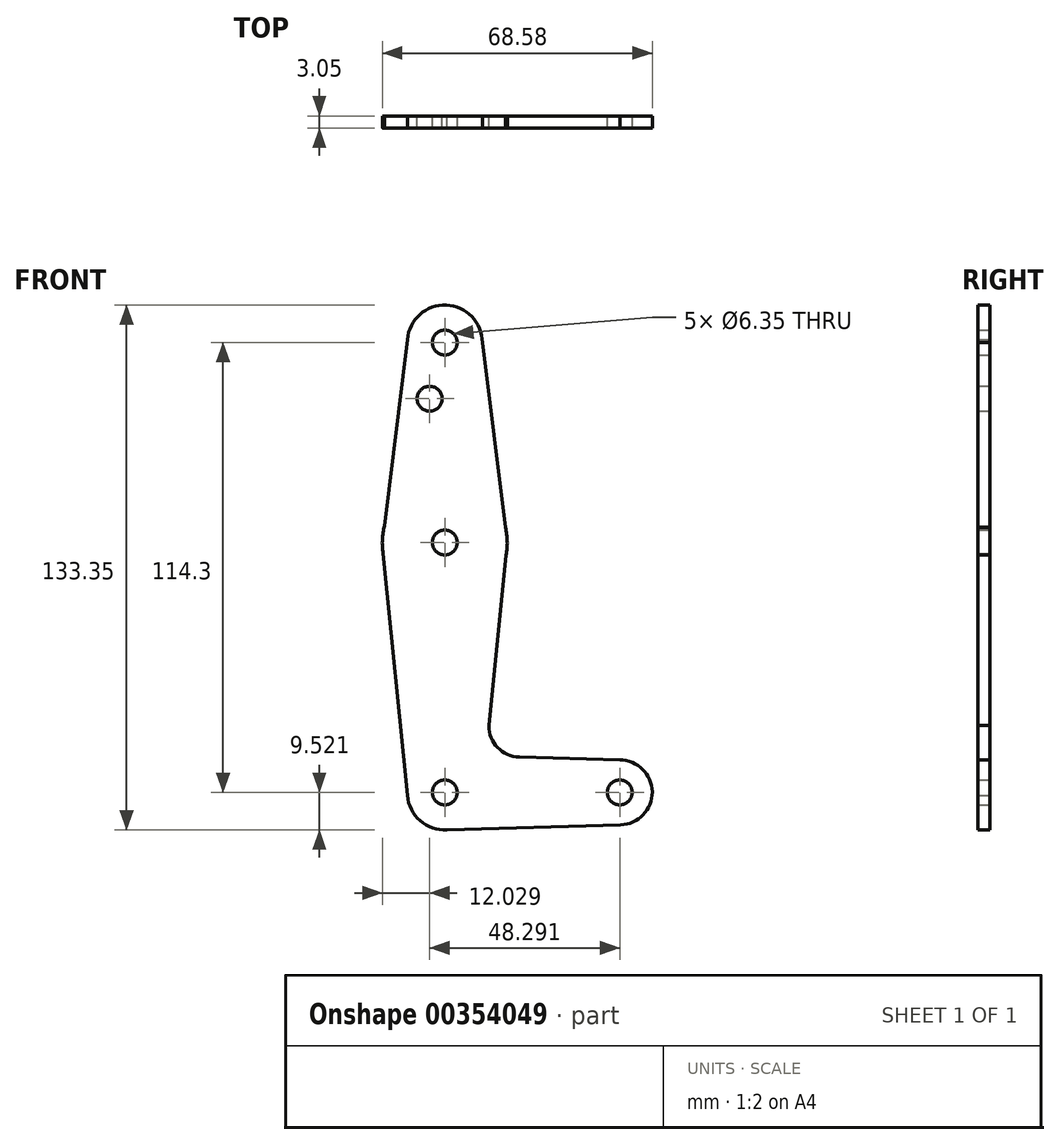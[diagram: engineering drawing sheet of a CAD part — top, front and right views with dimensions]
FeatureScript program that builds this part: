
annotation { "Feature Type Name" : "Feature", "Feature Type Description" : "" }
export const myFeature = defineFeature(function(context is Context, id is Id, definition is map)
    precondition{}
    {
        {
            var Q0;
            Q0=qCreatedBy(makeId("Front.planeOp"),FACE);
            var sketch = newSketch(context, id + "F0", { "sketchPlane" : qUnion([Q0])});
            skCircle(sketch, "E0", {"center": v(0, 55.41) * mm, "radius": 9.53 * mm});
            skCircle(sketch, "E1", {"center": v(0, 4.61) * mm, "radius": 15.88 * mm});
            skCircle(sketch, "E2", {"center": v(0, -58.89) * mm, "radius": 9.53 * mm});
            skCircle(sketch, "E3", {"center": v(44.45, -58.89) * mm, "radius": 8.26 * mm});
            skLineSegment(sketch, "E4", {"start": v(0, -58.89) * mm, "end": v(44.45, -58.89) * mm, "construction": true});
            skLineSegment(sketch, "E5", {"start": v(0, 55.41) * mm, "end": v(0, -58.89) * mm, "construction": true});
            skLineSegment(sketch, "E6", {"start": v(-9.5, 56.18) * mm, "end": v(-15.87, 4.2) * mm});
            skLineSegment(sketch, "E7", {"start": v(-9.5, -59.63) * mm, "end": v(9.53, -58.89) * mm});
            skLineSegment(sketch, "E8", {"start": v(-15.87, 4.2) * mm, "end": v(-9.5, -59.63) * mm});
            skLineSegment(sketch, "E9", {"start": v(41.03, -58.89) * mm, "end": v(41.42, -57.93) * mm});
            skLineSegment(sketch, "E10", {"start": v(44.45, -50.63) * mm, "end": v(18.94, -49.9) * mm});
            skCircle(sketch, "E11", {"center": v(0, 55.41) * mm, "radius": 3.18 * mm});
            skCircle(sketch, "E12", {"center": v(0, -58.89) * mm, "radius": 3.18 * mm});
            skCircle(sketch, "E13", {"center": v(0, 4.61) * mm, "radius": 3.18 * mm});
            skCircle(sketch, "E14", {"center": v(44.45, -58.89) * mm, "radius": 3.18 * mm});
            skCircle(sketch, "E15", {"center": v(-3.84, 41.14) * mm, "radius": 3.18 * mm});
            skPoint(sketch, "E16.newPointA", {"position": v(0.01, -49.36) * mm});
            skArc(sketch, "E16.filletArc", {"start": v(11.22, -41.9) * mm, "mid": v(13.45, -47.48) * mm, "end": v(18.94, -49.9) * mm});
            skLineSegment(sketch, "E17", {"start": v(15.87, 4.7) * mm, "end": v(11.22, -41.9) * mm});
            skLineSegment(sketch, "E18", {"start": v(9.52, 55.41) * mm, "end": v(15.87, 4.7) * mm});
            skLineSegment(sketch, "E19", {"start": v(0, -68.41) * mm, "end": v(44.69, -67.14) * mm});
            skSolve(sketch);
        }
        {
            var Q0;
            Q0 = qSketchRegion(id + "F0", true);
            extrude(context, id + "F1", {"entities" : qUnion([Q0]), "depth" : 3.05 * mm});
        }
    });
